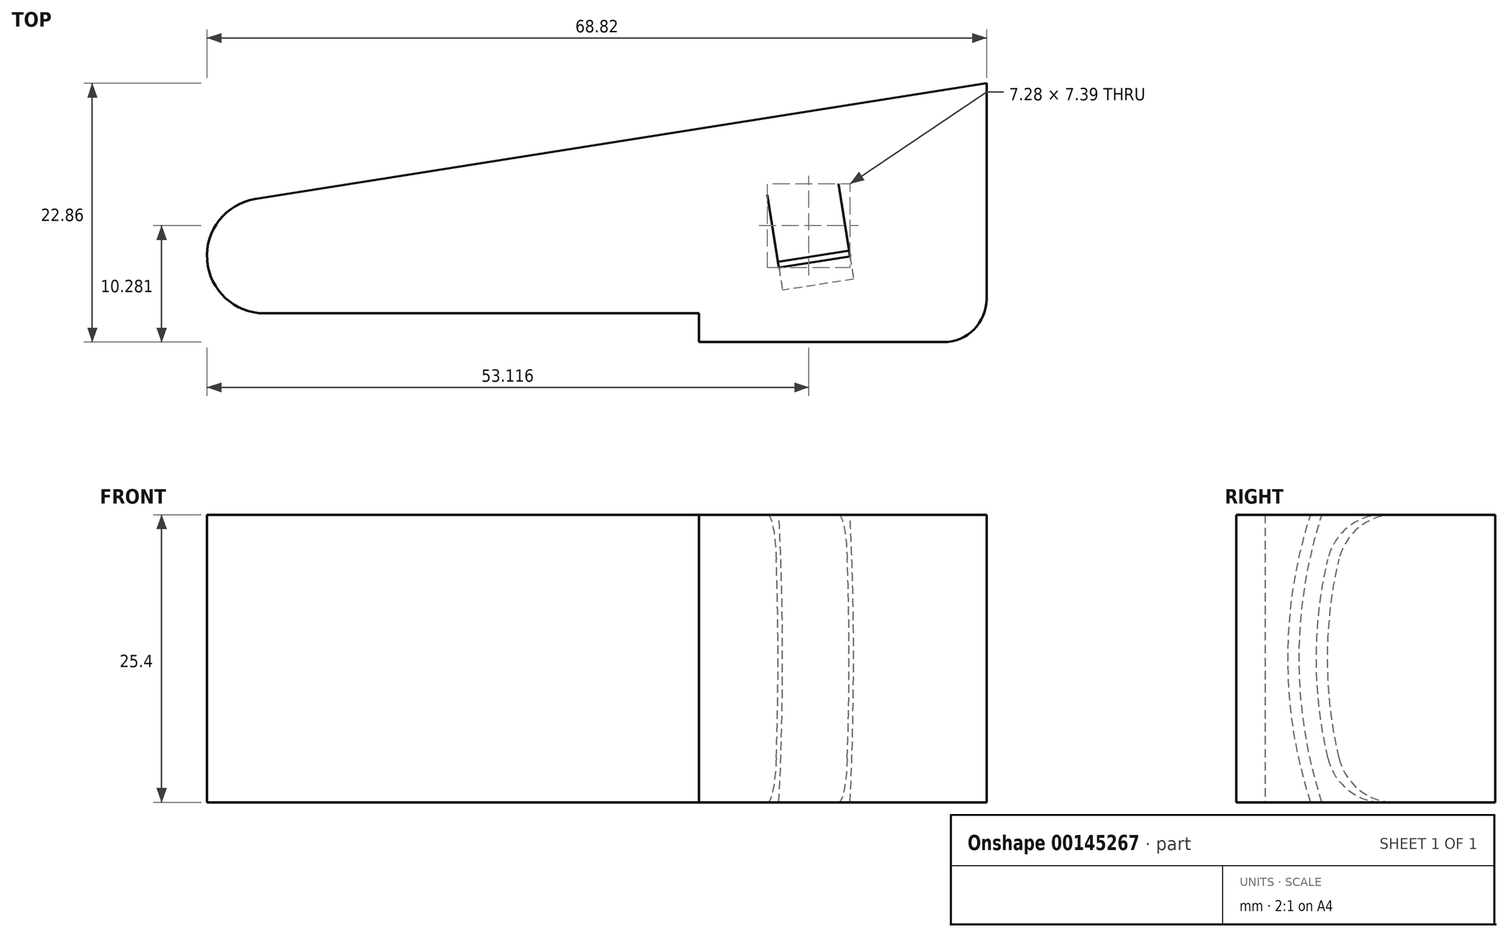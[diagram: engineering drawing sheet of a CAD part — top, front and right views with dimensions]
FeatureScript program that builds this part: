
annotation { "Feature Type Name" : "Feature", "Feature Type Description" : "" }
export const myFeature = defineFeature(function(context is Context, id is Id, definition is map)
    precondition{}
    {
        {
            var Q0;
            Q0=qCreatedBy(makeId("Top.planeOp"),FACE);
            var sketch = newSketch(context, id + "F0", { "sketchPlane" : qUnion([Q0])});
            skLineSegment(sketch, "E0", {"start": v(104.9, 2.54) * mm, "end": v(104.9, 22.86) * mm});
            skLineSegment(sketch, "E1", {"start": v(104.9, 22.86) * mm, "end": v(-23.4, 2.54) * mm});
            skPoint(sketch, "E2", {"position": v(79.5, 0) * mm});
            skLineSegment(sketch, "E3", {"start": v(79.5, 0) * mm, "end": v(79.5, 2.54) * mm});
            skPoint(sketch, "E4.orphan", {"position": v(104.9, 0) * mm});
            skLineSegment(sketch, "E5", {"start": v(104.9, 2.54) * mm, "end": v(104.9, 0) * mm});
            skLineSegment(sketch, "E6", {"start": v(104.9, 0) * mm, "end": v(79.5, 0) * mm});
            skLineSegment(sketch, "E7", {"start": v(79.5, 2.54) * mm, "end": v(-23.4, 2.54) * mm});
            skSolve(sketch);
        }
        {
            var Q0;
            Q0 = qSketchRegion(id + "F0", true);
            extrude(context, id + "F1", {"entities" : qUnion([Q0]), "depth" : 25.4 * mm});
        }
        {
            var Q0;
            Q0=makeQuery(id+"F1.opExtrude","SWEPT_EDGE",EDGE,{"disambiguationData":[OSD([sQuery(id+"F0.wireOp",EDGE,"E5"),sQuery(id+"F0.wireOp",EDGE,"E6")])]});
            fillet(context, id + "F2", {"entities" : qUnion([Q0]), "radius" : 3.8 * mm, "tangentPropagation" : true, "allowEdgeOverflow" : false});
        }
        {
            var Q0;
            Q0=makeQuery(id+"F1.opExtrude","SWEPT_FACE",FACE,{"disambiguationData":[OSD([sQuery(id+"F0.wireOp",EDGE,"E1")])]});
            var sketch = newSketch(context, id + "F3", { "sketchPlane" : qUnion([Q0])});
            skLineSegment(sketch, "E8.0.0", {"start": v(-25.7, 25.4) * mm, "end": v(-102.73, 25.4) * mm});
            skLineSegment(sketch, "E8.0.1", {"start": v(-102.73, 25.4) * mm, "end": v(-102.73, 0) * mm});
            skLineSegment(sketch, "E8.0.2", {"start": v(-102.73, 0) * mm, "end": v(-25.7, 0) * mm});
            skLineSegment(sketch, "E8.0.3", {"start": v(-25.7, 0) * mm, "end": v(-25.7, 25.4) * mm});
            skPoint(sketch, "E9", {"position": v(-102.73, 12.7) * mm});
            skPoint(sketch, "E10", {"position": v(-25.7, 12.7) * mm});
            skLineSegment(sketch, "E11", {"start": v(-102.73, 12.7) * mm, "end": v(-25.7, 12.7) * mm});
            skSolve(sketch);
        }
        {
            var Q0;
            {var subQ0=sQuery(id+"F3.wireOp",EDGE,"E8.0.0");Q0=makeQuery(id+"F3.imprint","IMPRINT",FACE,{"disambiguationData":[TD([[makeQuery(id+"F3.imprint","IMPRINT",EDGE,{"derivedFrom":subQ0}),-1.0]])]});}
            cPlane(context, id + "F4", {"entities" : qUnion([Q0]), "cplaneType" : CPlaneType.OFFSET, "offset" : 25.4 * mm, "width" : 152.4 * mm, "height" : 152.4 * mm});
        }
        {
            var Q0;
            Q0=qCreatedBy(id+"F4.planeOp",FACE);
            var sketch = newSketch(context, id + "F5", { "sketchPlane" : qUnion([Q0])});
            skLineSegment(sketch, "E12.0", {"start": v(-102.73, 12.7) * mm, "end": v(-25.7, 12.7) * mm, "construction": true});
            skLineSegment(sketch, "E13.0", {"start": v(-78.92, 25.4) * mm, "end": v(-78.92, 0) * mm, "construction": true});
            skLineSegment(sketch, "E14.bottom", {"start": v(-92.88, 53.34) * mm, "end": v(-86.53, 53.34) * mm});
            skLineSegment(sketch, "E14.top", {"start": v(-92.88, 50.8) * mm, "end": v(-86.53, 50.8) * mm});
            skLineSegment(sketch, "E14.left", {"start": v(-92.88, 53.34) * mm, "end": v(-92.88, 50.8) * mm});
            skLineSegment(sketch, "E14.right", {"start": v(-86.53, 53.34) * mm, "end": v(-86.53, 50.8) * mm});
            skSolve(sketch);
        }
        {
            var Q0;
            Q0 = qSketchRegion(id + "F5", true);
            var Q1;
            Q1=sQuery(id+"F5.wireOp",EDGE,"E12.0");
            revolve(context, id + "F6", {"operationType" : NewBodyOperationType.REMOVE, "entities" : qUnion([Q0]), "axis" : qUnion([Q1]), "revolveType" : RevolveType.FULL, "oppositeDirection" : true});
        }
        {
            var Q0;
            Q0=makeQuery(id+"F6.boolean.opBoolean","INTERSECT",EDGE,{"derivedFrom":[makeQuery(id+"F1.opExtrude","CAP_FACE",FACE,{"disambiguationData":[OSD([sQuery(id+"F0.wireOp",EDGE,"E0"),sQuery(id+"F0.wireOp",EDGE,"E1"),sQuery(id+"F0.wireOp",EDGE,"E3"),sQuery(id+"F0.wireOp",EDGE,"E5"),sQuery(id+"F0.wireOp",EDGE,"E6"),sQuery(id+"F0.wireOp",EDGE,"E7")])],"isStart":false}),makeQuery(id+"F6.opRevolve","SWEPT_FACE",FACE,{"disambiguationData":[OSD([sQuery(id+"F5.wireOp",EDGE,"E14.top")])]})]});
            var Q1;
            Q1=makeQuery(id+"F6.boolean.opBoolean","INTERSECT",EDGE,{"derivedFrom":[makeQuery(id+"F1.opExtrude","CAP_FACE",FACE,{"disambiguationData":[OSD([sQuery(id+"F0.wireOp",EDGE,"E0"),sQuery(id+"F0.wireOp",EDGE,"E1"),sQuery(id+"F0.wireOp",EDGE,"E3"),sQuery(id+"F0.wireOp",EDGE,"E5"),sQuery(id+"F0.wireOp",EDGE,"E6"),sQuery(id+"F0.wireOp",EDGE,"E7")])],"isStart":true}),makeQuery(id+"F6.opRevolve","SWEPT_FACE",FACE,{"disambiguationData":[OSD([sQuery(id+"F5.wireOp",EDGE,"E14.top")])]})]});
            fillet(context, id + "F7", {"entities" : qUnion([Q0, Q1]), "radius" : 5.08 * mm, "tangentPropagation" : true, "allowEdgeOverflow" : false});
        }
        {
            var Q0;
            Q0=makeQuery(id+"F1.opExtrude","SWEPT_EDGE",EDGE,{"disambiguationData":[OSD([sQuery(id+"F0.wireOp",EDGE,"E1"),sQuery(id+"F0.wireOp",EDGE,"E7")])]});
            fillet(context, id + "F8", {"entities" : qUnion([Q0]), "radius" : 5.08 * mm, "tangentPropagation" : true, "allowEdgeOverflow" : false});
        }
    });
